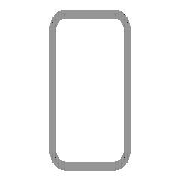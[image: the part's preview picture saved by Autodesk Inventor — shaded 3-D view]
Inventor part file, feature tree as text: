
AUTODESK INVENTOR PART (.ipt)
format: ipt  version: 2025 (Build 290162010, 162A)  size: 131,584 bytes
history: native  units: mm (DEFAULTED — no unit token found)
features: other x4, sketch x1, plane x1
ambient origin geometry x8: Origin, YZ Plane, XZ Plane, XY Plane, X Axis, Y Axis, Z Axis, Center Point
bodies: Solid1 (feature_tree), Body (feature_tree)
feature tree (6):
  parser-record x1  (decoder bookkeeping rows leaked as tree rows — omitted from the tree; the rows remain in map.json)
  other  "Driven Length"
  other  "Start Plane"
  other  "End Plane"
  sketch  "Sketch3"  dims[d3=2200.0mm d4=0.0mm d7=6.0mm d9=40.0mm d11=80.0mm d12=3.0mm d13=-0.0mm d14=2200.0mm d15=20.0mm d16=40.0mm d17=90.0deg d18=2200.0mm]
  plane  "Work Plane3"
